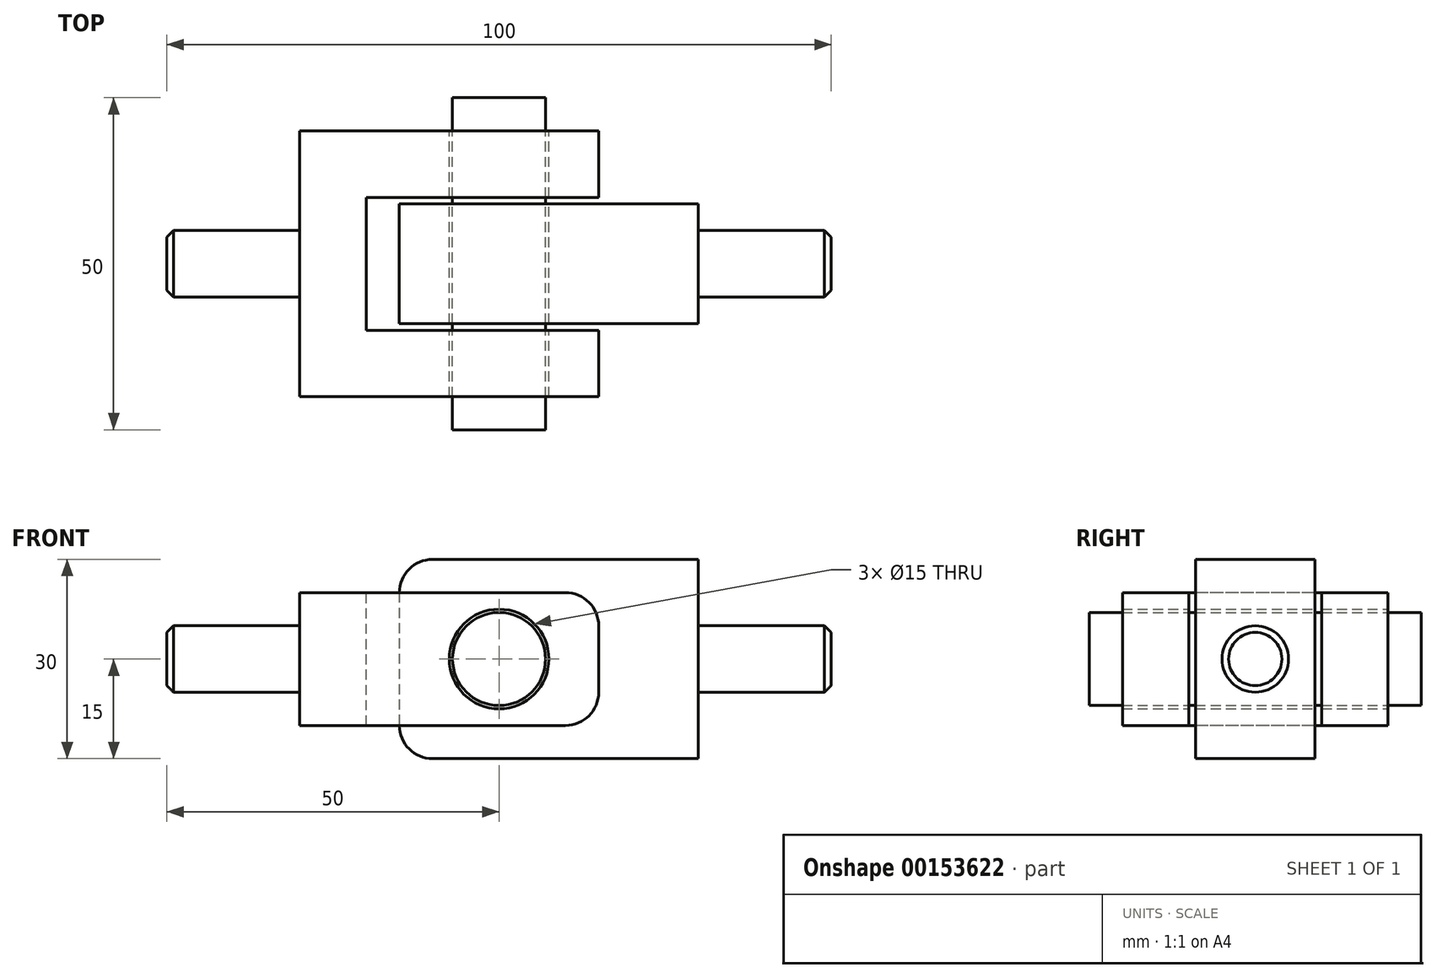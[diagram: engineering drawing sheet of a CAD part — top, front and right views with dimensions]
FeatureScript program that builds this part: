
annotation { "Feature Type Name" : "Feature", "Feature Type Description" : "" }
export const myFeature = defineFeature(function(context is Context, id is Id, definition is map)
    precondition{}
    {
        {
            var Q0;
            Q0=qCreatedBy(makeId("Right.planeOp"),FACE);
            var sketch = newSketch(context, id + "F0", { "sketchPlane" : qUnion([Q0])});
            skLineSegment(sketch, "E0.bottom", {"start": v(0, 0) * mm, "end": v(-40, 0) * mm});
            skLineSegment(sketch, "E0.top", {"start": v(0, -20) * mm, "end": v(-40, -20) * mm});
            skLineSegment(sketch, "E0.left", {"start": v(0, 0) * mm, "end": v(0, -20) * mm});
            skLineSegment(sketch, "E0.right", {"start": v(-40, 0) * mm, "end": v(-40, -20) * mm});
            skCircle(sketch, "E1", {"center": v(-20, -10) * mm, "radius": 5 * mm});
            skSolve(sketch);
        }
        {
            var Q0;
            Q0=makeQuery(id+"F0.imprint","IMPRINT",FACE,{"disambiguationData":[TD([[makeQuery(id+"F0.imprint","IMPRINT",EDGE,{"derivedFrom":sQuery(id+"F0.wireOp",EDGE,"E1")}),1.0]])]});
            extrude(context, id + "F1", {"entities" : qUnion([Q0]), "oppositeDirection" : true, "depth" : 20 * mm});
        }
        {
            var Q0;
            Q0=qCreatedBy(makeId("Top.planeOp"),FACE);
            var sketch = newSketch(context, id + "F2", { "sketchPlane" : qUnion([Q0])});
            skLineSegment(sketch, "E2.bottom", {"start": v(0, 0) * mm, "end": v(45, 0) * mm});
            skLineSegment(sketch, "E2.top", {"start": v(0, -40) * mm, "end": v(45, -40) * mm});
            skLineSegment(sketch, "E2.left", {"start": v(0, 0) * mm, "end": v(0, -40) * mm});
            skLineSegment(sketch, "E2.right", {"start": v(45, 0) * mm, "end": v(45, -40) * mm});
            skLineSegment(sketch, "E3.bottom", {"start": v(45, -10) * mm, "end": v(10, -10) * mm});
            skLineSegment(sketch, "E3.top", {"start": v(45, -30) * mm, "end": v(10, -30) * mm});
            skLineSegment(sketch, "E3.left", {"start": v(45, -10) * mm, "end": v(45, -30) * mm});
            skLineSegment(sketch, "E3.right", {"start": v(10, -10) * mm, "end": v(10, -30) * mm});
            skPoint(sketch, "E4.startSnap0", {"position": v(22.5, 0) * mm});
            skPoint(sketch, "E4.endSnap0", {"position": v(27.5, -10) * mm});
            skLineSegment(sketch, "E5", {"start": v(15, -10) * mm, "end": v(15, -30) * mm});
            skLineSegment(sketch, "E6", {"start": v(15, -30) * mm, "end": v(60, -30) * mm});
            skLineSegment(sketch, "E7", {"start": v(60, -30) * mm, "end": v(60, -10) * mm});
            skLineSegment(sketch, "E8", {"start": v(60, -10) * mm, "end": v(15, -10) * mm});
            skSolve(sketch);
        }
        {
            var Q0;
            {var subQ0=sQuery(id+"F2.wireOp",EDGE,"E2.left");Q0=makeQuery(id+"F2.imprint","IMPRINT",FACE,{"disambiguationData":[TD([[makeQuery(id+"F2.imprint","IMPRINT",EDGE,{"derivedFrom":subQ0}),1.0]])]});}
            var Q1;
            {var subQ0=sQuery(id+"F2.wireOp",EDGE,"lwf0jP7u-qRGJ-sjRD-eBDz-npzYwXVrge2I");var subQ1=sQuery(id+"F2.wireOp",EDGE,"E2.bottom");var subQ2=makeQuery(id+"F2.imprint","INTERSECT",VERTEX,{"derivedFrom":[subQ1,subQ0]});Q1=makeQuery(id+"F2.imprint","IMPRINT",FACE,{"disambiguationData":[TD([[makeQuery(id+"F2.imprint","IMPRINT",EDGE,{"disambiguationData":[TD([[subQ2,1.0]])],"derivedFrom":subQ1}),-1.0]])]});}
            var Q2;
            {var subQ0=sQuery(id+"F2.wireOp",EDGE,"E2.right");var subQ1=sQuery(id+"F2.wireOp",EDGE,"E2.bottom");var subQ2=makeQuery(id+"F2.imprint","INTERSECT",VERTEX,{"derivedFrom":[subQ1,subQ0]});Q2=makeQuery(id+"F2.imprint","IMPRINT",FACE,{"disambiguationData":[TD([[makeQuery(id+"F2.imprint","IMPRINT",EDGE,{"disambiguationData":[TD([[subQ2,1.0]])],"derivedFrom":subQ1}),-1.0]])]});}
            var Q3;
            {var subQ0=sQuery(id+"F2.wireOp",EDGE,"E2.right");var subQ1=sQuery(id+"F2.wireOp",EDGE,"E2.top");var subQ2=makeQuery(id+"F2.imprint","INTERSECT",VERTEX,{"derivedFrom":[subQ1,subQ0]});Q3=makeQuery(id+"F2.imprint","IMPRINT",FACE,{"disambiguationData":[TD([[makeQuery(id+"F2.imprint","IMPRINT",EDGE,{"disambiguationData":[TD([[subQ2,1.0]])],"derivedFrom":subQ1}),1.0]])]});}
            var Q4;
            {var subQ0=sQuery(id+"F2.wireOp",EDGE,"lwf0jP7u-qRGJ-sjRD-eBDz-npzYwXVrge2I");var subQ1=sQuery(id+"F2.wireOp",EDGE,"E2.top");var subQ2=makeQuery(id+"F2.imprint","INTERSECT",VERTEX,{"derivedFrom":[subQ1,subQ0]});Q4=makeQuery(id+"F2.imprint","IMPRINT",FACE,{"disambiguationData":[TD([[makeQuery(id+"F2.imprint","IMPRINT",EDGE,{"disambiguationData":[TD([[subQ2,1.0]])],"derivedFrom":subQ1}),1.0]])]});}
            extrude(context, id + "F3", {"entities" : qUnion([Q0, Q1, Q2, Q3, Q4]), "oppositeDirection" : true, "depth" : 20 * mm});
        }
        {
            var Q0;
            {var subQ0=sQuery(id+"F2.wireOp",EDGE,"E2.right");Q0=makeQuery(id+"F3.opExtrude","CAP_EDGE",EDGE,{"disambiguationData":[OSD([subQ0]),TDD([makeQuery(id+"F2.imprint","IMPRINT",EDGE,{"disambiguationData":[TD([[makeQuery(id+"F2.imprint","INTERSECT",VERTEX,{"derivedFrom":[sQuery(id+"F2.wireOp",EDGE,"E2.top"),subQ0]}),1.0]])],"derivedFrom":subQ0})])],"isStart":true});}
            var Q1;
            {var subQ0=sQuery(id+"F2.wireOp",EDGE,"E2.right");Q1=makeQuery(id+"F3.opExtrude","CAP_EDGE",EDGE,{"disambiguationData":[OSD([subQ0]),TDD([makeQuery(id+"F2.imprint","IMPRINT",EDGE,{"disambiguationData":[TD([[makeQuery(id+"F2.imprint","INTERSECT",VERTEX,{"derivedFrom":[sQuery(id+"F2.wireOp",EDGE,"E2.bottom"),subQ0]}),-1.0]])],"derivedFrom":subQ0})])],"isStart":true});}
            var Q2;
            {var subQ0=sQuery(id+"F2.wireOp",EDGE,"E2.right");Q2=makeQuery(id+"F3.opExtrude","CAP_EDGE",EDGE,{"disambiguationData":[OSD([subQ0]),TDD([makeQuery(id+"F2.imprint","IMPRINT",EDGE,{"disambiguationData":[TD([[makeQuery(id+"F2.imprint","INTERSECT",VERTEX,{"derivedFrom":[sQuery(id+"F2.wireOp",EDGE,"E2.top"),subQ0]}),1.0]])],"derivedFrom":subQ0})])],"isStart":false});}
            var Q3;
            {var subQ0=sQuery(id+"F2.wireOp",EDGE,"E2.right");Q3=makeQuery(id+"F3.opExtrude","CAP_EDGE",EDGE,{"disambiguationData":[OSD([subQ0]),TDD([makeQuery(id+"F2.imprint","IMPRINT",EDGE,{"disambiguationData":[TD([[makeQuery(id+"F2.imprint","INTERSECT",VERTEX,{"derivedFrom":[sQuery(id+"F2.wireOp",EDGE,"E2.bottom"),subQ0]}),-1.0]])],"derivedFrom":subQ0})])],"isStart":false});}
            fillet(context, id + "F4", {"entities" : qUnion([Q0, Q1, Q2, Q3]), "radius" : 5 * mm, "tangentPropagation" : true, "allowEdgeOverflow" : false});
        }
        {
            var Q0;
            Q0=qCreatedBy(makeId("Front.planeOp"),FACE);
            var sketch = newSketch(context, id + "F5", { "sketchPlane" : qUnion([Q0])});
            skCircle(sketch, "E9", {"center": v(30, -10) * mm, "radius": 7.5 * mm});
            skLineSegment(sketch, "E10", {"start": v(15, 5) * mm, "end": v(15, -25) * mm});
            skLineSegment(sketch, "E11", {"start": v(15, -25) * mm, "end": v(60, -25) * mm});
            skLineSegment(sketch, "E12", {"start": v(60, -25) * mm, "end": v(60, 5) * mm});
            skLineSegment(sketch, "E13", {"start": v(60, 5) * mm, "end": v(15, 5) * mm});
            skLineSegment(sketch, "E14", {"start": v(60, -5) * mm, "end": v(80, -5) * mm});
            skLineSegment(sketch, "E15", {"start": v(80, -5) * mm, "end": v(80, -15) * mm});
            skLineSegment(sketch, "E16", {"start": v(80, -15) * mm, "end": v(60, -15) * mm});
            skCircle(sketch, "E17", {"center": v(30, -10) * mm, "radius": 7 * mm});
            skSolve(sketch);
        }
        {
            var Q0;
            Q0=sQuery(id+"F5.wireOp",VERTEX,"E9.center");
            var Q1;
            Q1=makeQuery(id+"F3.opExtrude","SWEPT_BODY",BODY,{"disambiguationData":[OSD([sQuery(id+"F2.wireOp",EDGE,"E2.bottom"),sQuery(id+"F2.wireOp",EDGE,"E2.top"),sQuery(id+"F2.wireOp",EDGE,"E2.left"),sQuery(id+"F2.wireOp",EDGE,"E2.right"),sQuery(id+"F2.wireOp",EDGE,"E3.bottom"),sQuery(id+"F2.wireOp",EDGE,"E3.top"),sQuery(id+"F2.wireOp",EDGE,"E3.right")])]});
            hole(context, id + "F6", {"style" : HoleStyle.SIMPLE, "endStyle" : HoleEndStyle.THROUGH, "oppositeDirection" : true, "holeDiameter" : 15 * mm, "locations" : qUnion([Q0]), "scope" : qUnion([Q1]), "isTappedThrough" : true});
        }
        {
            var Q0;
            Q0=makeQuery(id+"F1.opExtrude","CAP_FACE",FACE,{"disambiguationData":[OSD([sQuery(id+"F0.wireOp",EDGE,"E1")])],"isStart":false});
            chamfer(context, id + "F7", {"entities" : qUnion([Q0]), "width" : 1 * mm, "tangentPropagation" : true});
        }
        {
            var Q0;
            Q0=makeQuery(id+"F5.imprint","IMPRINT",FACE,{"disambiguationData":[TD([[makeQuery(id+"F5.imprint","IMPRINT",EDGE,{"derivedFrom":sQuery(id+"F5.wireOp",EDGE,"E17")}),1.0]])]});
            extrude(context, id + "F8", {"entities" : qUnion([Q0]), "operationType" : NewBodyOperationType.ADD, "depth" : 45 * mm, "hasSecondDirection" : true, "secondDirectionOppositeDirection" : true, "secondDirectionDepth" : 5 * mm});
        }
        {
            var Q0;
            Q0=makeQuery(id+"F5.imprint","IMPRINT",FACE,{"disambiguationData":[TD([[makeQuery(id+"F5.imprint","IMPRINT",EDGE,{"derivedFrom":sQuery(id+"F5.wireOp",EDGE,"E9")}),-1.0]])]});
            extrude(context, id + "F9", {"entities" : qUnion([Q0]), "operationType" : NewBodyOperationType.ADD, "depth" : 29 * mm, "hasSecondDirection" : true, "secondDirectionOppositeDirection" : false, "secondDirectionDepth" : 11 * mm});
        }
        {
            var Q0;
            Q0=makeQuery(id+"F9.opExtrude","SWEPT_EDGE",EDGE,{"disambiguationData":[OSD([sQuery(id+"F5.wireOp",EDGE,"E10"),sQuery(id+"F5.wireOp",EDGE,"E13")])]});
            var Q1;
            Q1=makeQuery(id+"F9.opExtrude","SWEPT_EDGE",EDGE,{"disambiguationData":[OSD([sQuery(id+"F5.wireOp",EDGE,"E10"),sQuery(id+"F5.wireOp",EDGE,"E11")])]});
            fillet(context, id + "F10", {"entities" : qUnion([Q0, Q1]), "radius" : 5 * mm, "tangentPropagation" : true, "allowEdgeOverflow" : false});
        }
        {
            var Q0;
            {var subQ0=sQuery(id+"F5.wireOp",EDGE,"E14");Q0=makeQuery(id+"F5.imprint","IMPRINT",FACE,{"disambiguationData":[TD([[makeQuery(id+"F5.imprint","IMPRINT",EDGE,{"derivedFrom":subQ0}),-1.0]])]});}
            extrude(context, id + "F11", {"entities" : qUnion([Q0]), "operationType" : NewBodyOperationType.ADD, "depth" : 25 * mm, "hasSecondDirection" : true, "secondDirectionOppositeDirection" : false, "secondDirectionDepth" : 15 * mm});
        }
        {
            var Q0;
            Q0=makeQuery(id+"F11.opExtrude","CAP_EDGE",EDGE,{"disambiguationData":[OSD([sQuery(id+"F5.wireOp",EDGE,"E14")])],"isStart":false});
            var Q1;
            Q1=makeQuery(id+"F11.opExtrude","CAP_EDGE",EDGE,{"disambiguationData":[OSD([sQuery(id+"F5.wireOp",EDGE,"E14")])],"isStart":true});
            var Q2;
            Q2=makeQuery(id+"F11.opExtrude","CAP_EDGE",EDGE,{"disambiguationData":[OSD([sQuery(id+"F5.wireOp",EDGE,"E16")])],"isStart":true});
            var Q3;
            Q3=makeQuery(id+"F11.opExtrude","CAP_EDGE",EDGE,{"disambiguationData":[OSD([sQuery(id+"F5.wireOp",EDGE,"E16")])],"isStart":false});
            fillet(context, id + "F12", {"entities" : qUnion([Q0, Q1, Q2, Q3]), "radius" : 5 * mm, "tangentPropagation" : true, "allowEdgeOverflow" : false});
        }
        {
            var Q0;
            Q0=makeQuery(id+"F11.opExtrude","SWEPT_FACE",FACE,{"disambiguationData":[OSD([sQuery(id+"F5.wireOp",EDGE,"E15")])]});
            chamfer(context, id + "F13", {"entities" : qUnion([Q0]), "width" : 1 * mm, "tangentPropagation" : true});
        }
    });
